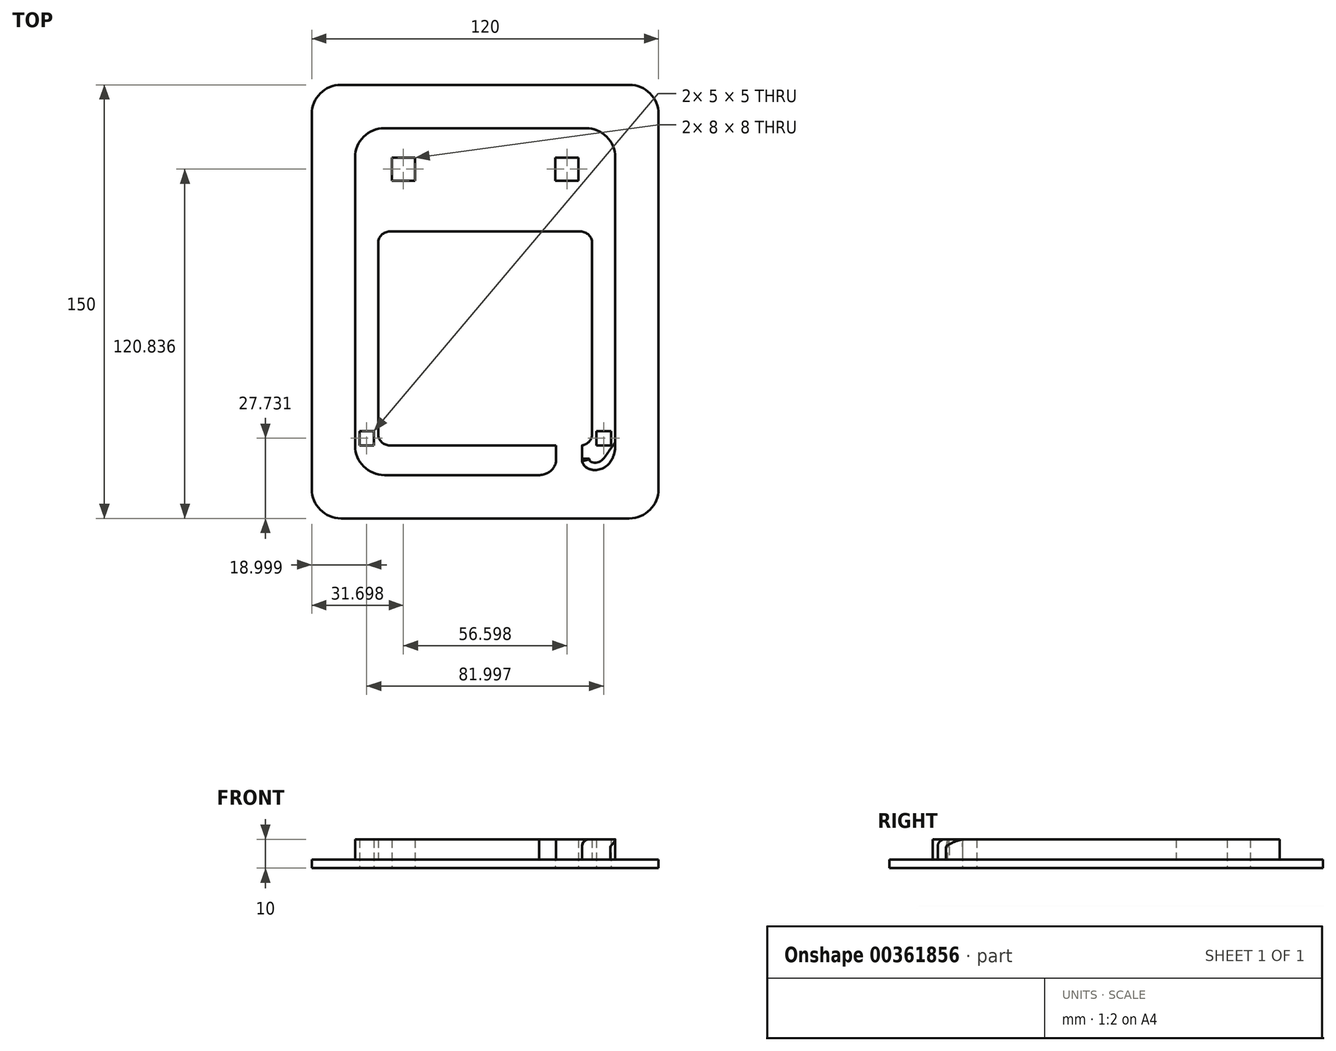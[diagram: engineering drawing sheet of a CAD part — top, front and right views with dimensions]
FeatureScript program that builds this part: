
annotation { "Feature Type Name" : "Feature", "Feature Type Description" : "" }
export const myFeature = defineFeature(function(context is Context, id is Id, definition is map)
    precondition{}
    {
        {
            var Q0;
            Q0=qCreatedBy(makeId("Top.planeOp"),FACE);
            var sketch = newSketch(context, id + "F0", { "sketchPlane" : qUnion([Q0])});
            skLineSegment(sketch, "E0", {"start": v(-11.46, -28.66) * mm, "end": v(-11.46, -18.43) * mm, "construction": true});
            skArc(sketch, "E1.0", {"start": v(28.36, -28.66) * mm, "mid": v(33.6, -27.2) * mm, "end": v(37.34, -23.25) * mm});
            skFitSpline(sketch, "E1.1", {"points": [v(27, -22.97) * mm, v(27, -23.26) * mm, v(27.03, -23.7) * mm, v(27.19, -24.26) * mm, v(27.36, -24.67) * mm, v(27.57, -25.04) * mm, v(27.93, -25.51) * mm, v(28.35, -25.9) * mm, v(28.84, -26.24) * mm, v(29.23, -26.44) * mm, v(29.63, -26.6) * mm, v(30.19, -26.79) * mm, v(30.9, -26.92) * mm, v(31.78, -26.94) * mm, v(32.64, -26.83) * mm, v(33.5, -26.6) * mm, v(34.3, -26.27) * mm, v(35.05, -25.83) * mm, v(35.74, -25.3) * mm, v(36.36, -24.7) * mm, v(36.9, -24) * mm, v(37.2, -23.5) * mm, v(37.34, -23.25) * mm]});
            skLineSegment(sketch, "E1.2", {"start": v(-43.48, -14.43) * mm, "end": v(-43.48, 51.57) * mm});
            skArc(sketch, "E1.3", {"start": v(-56.32, 106.34) * mm, "mid": v(-63.5, 103.36) * mm, "end": v(-66.48, 96.18) * mm});
            skArc(sketch, "E1.4", {"start": v(43.36, -43.66) * mm, "mid": v(50.54, -40.69) * mm, "end": v(53.52, -33.5) * mm});
            skLineSegment(sketch, "E1.5", {"start": v(-39.48, 51.57) * mm, "end": v(-43.48, 51.57) * mm});
            skArc(sketch, "E1.6", {"start": v(-66.48, -33.5) * mm, "mid": v(-63.5, -40.69) * mm, "end": v(-56.32, -43.66) * mm});
            skArc(sketch, "E1.7", {"start": v(-41.32, 91.34) * mm, "mid": v(-48.5, 88.36) * mm, "end": v(-51.48, 81.18) * mm});
            skLineSegment(sketch, "E1.8", {"start": v(18.05, -23.58) * mm, "end": v(25.68, -23.58) * mm});
            skArc(sketch, "E1.9", {"start": v(38.52, 81.18) * mm, "mid": v(35.54, 88.36) * mm, "end": v(28.36, 91.34) * mm});
            skArc(sketch, "E1.10", {"start": v(-51.48, -18.5) * mm, "mid": v(-48.5, -25.69) * mm, "end": v(-41.32, -28.66) * mm});
            skLineSegment(sketch, "E2.0.0", {"start": v(-66.48, 96.18) * mm, "end": v(-66.48, -33.5) * mm});
            skLineSegment(sketch, "E2.0.2", {"start": v(-56.32, -43.66) * mm, "end": v(43.36, -43.66) * mm});
            skLineSegment(sketch, "E2.0.4", {"start": v(53.52, -33.5) * mm, "end": v(53.52, 96.18) * mm});
            skArc(sketch, "E2.0.5", {"start": v(53.52, 96.18) * mm, "mid": v(50.54, 103.36) * mm, "end": v(43.36, 106.34) * mm});
            skLineSegment(sketch, "E2.0.6", {"start": v(43.36, 106.34) * mm, "end": v(-56.32, 106.34) * mm});
            skLineSegment(sketch, "E3.0.0", {"start": v(27, -18.4) * mm, "end": v(27, -22.97) * mm});
            skFitSpline(sketch, "E3.0.1", {"points": [v(27, -22.97) * mm, v(27, -23.26) * mm, v(27.03, -23.7) * mm, v(27.19, -24.26) * mm, v(27.36, -24.67) * mm, v(27.57, -25.04) * mm, v(27.93, -25.51) * mm, v(28.35, -25.9) * mm, v(28.84, -26.24) * mm, v(29.23, -26.44) * mm, v(29.63, -26.6) * mm, v(30.19, -26.79) * mm, v(30.9, -26.92) * mm, v(31.78, -26.94) * mm, v(32.64, -26.83) * mm, v(33.5, -26.6) * mm, v(34.3, -26.27) * mm, v(35.05, -25.83) * mm, v(35.74, -25.3) * mm, v(36.36, -24.7) * mm, v(36.9, -24) * mm, v(37.2, -23.5) * mm, v(37.34, -23.25) * mm]});
            skArc(sketch, "E3.0.2", {"start": v(37.34, -23.25) * mm, "mid": v(38.22, -20.95) * mm, "end": v(38.52, -18.5) * mm});
            skLineSegment(sketch, "E3.0.3", {"start": v(38.52, -18.5) * mm, "end": v(38.52, 81.18) * mm});
            skLineSegment(sketch, "E3.0.5", {"start": v(28.36, 91.34) * mm, "end": v(-41.32, 91.34) * mm});
            skLineSegment(sketch, "E3.0.7", {"start": v(-51.48, 81.18) * mm, "end": v(-51.48, -18.5) * mm});
            skLineSegment(sketch, "E3.0.9", {"start": v(-41.32, -28.66) * mm, "end": v(12.19, -28.66) * mm});
            skFitSpline(sketch, "E3.0.10", {"points": [v(12.19, -28.66) * mm, v(12.54, -28.66) * mm, v(13.07, -28.61) * mm, v(13.76, -28.46) * mm, v(14.27, -28.3) * mm, v(14.77, -28.1) * mm, v(15.24, -27.85) * mm, v(15.69, -27.57) * mm, v(16.12, -27.24) * mm, v(16.52, -26.89) * mm, v(16.88, -26.5) * mm, v(17.2, -26.09) * mm, v(17.5, -25.63) * mm, v(17.73, -25.15) * mm, v(17.9, -24.65) * mm, v(18.02, -24.12) * mm, v(18.05, -23.76) * mm, v(18.05, -23.58) * mm]});
            skLineSegment(sketch, "E3.0.11", {"start": v(18.05, -23.58) * mm, "end": v(18.05, -18.43) * mm});
            skLineSegment(sketch, "E3.0.12", {"start": v(18.05, -18.43) * mm, "end": v(-39.48, -18.43) * mm});
            skArc(sketch, "E3.0.13", {"start": v(-39.48, -18.43) * mm, "mid": v(-42.31, -17.26) * mm, "end": v(-43.48, -14.43) * mm});
            skArc(sketch, "E3.0.15", {"start": v(-43.48, 51.57) * mm, "mid": v(-42.31, 54.4) * mm, "end": v(-39.48, 55.57) * mm});
            skLineSegment(sketch, "E3.0.16", {"start": v(-39.48, 55.57) * mm, "end": v(26.52, 55.57) * mm});
            skArc(sketch, "E3.0.17", {"start": v(26.52, 55.57) * mm, "mid": v(29.35, 54.4) * mm, "end": v(30.52, 51.57) * mm});
            skLineSegment(sketch, "E3.0.18", {"start": v(30.52, 51.57) * mm, "end": v(30.52, -14.43) * mm});
            skArc(sketch, "E3.0.19", {"start": v(30.52, -14.43) * mm, "mid": v(29.5, -17.08) * mm, "end": v(27, -18.4) * mm});
            skLineSegment(sketch, "E4.0.0", {"start": v(-38.78, 81.18) * mm, "end": v(-38.78, 73.18) * mm});
            skLineSegment(sketch, "E4.0.1", {"start": v(-38.78, 73.18) * mm, "end": v(-30.78, 73.18) * mm});
            skLineSegment(sketch, "E4.0.2", {"start": v(-30.78, 73.18) * mm, "end": v(-30.78, 81.18) * mm});
            skLineSegment(sketch, "E4.0.3", {"start": v(-30.78, 81.18) * mm, "end": v(-38.78, 81.18) * mm});
            skLineSegment(sketch, "E5.0.0", {"start": v(25.82, 73.18) * mm, "end": v(25.82, 81.18) * mm});
            skLineSegment(sketch, "E5.0.1", {"start": v(25.82, 81.18) * mm, "end": v(17.82, 81.18) * mm});
            skLineSegment(sketch, "E5.0.2", {"start": v(17.82, 81.18) * mm, "end": v(17.82, 73.18) * mm});
            skLineSegment(sketch, "E5.0.3", {"start": v(17.82, 73.18) * mm, "end": v(25.82, 73.18) * mm});
            skLineSegment(sketch, "E6.0.0", {"start": v(-44.98, -18.43) * mm, "end": v(-44.98, -13.43) * mm});
            skLineSegment(sketch, "E6.0.1", {"start": v(-44.98, -13.43) * mm, "end": v(-49.98, -13.43) * mm});
            skLineSegment(sketch, "E6.0.2", {"start": v(-49.98, -13.43) * mm, "end": v(-49.98, -18.43) * mm});
            skLineSegment(sketch, "E6.0.3", {"start": v(-49.98, -18.43) * mm, "end": v(-44.98, -18.43) * mm});
            skLineSegment(sketch, "E7.0.0", {"start": v(32.02, -13.43) * mm, "end": v(32.02, -18.43) * mm});
            skLineSegment(sketch, "E7.0.1", {"start": v(32.02, -18.43) * mm, "end": v(37.02, -18.43) * mm});
            skLineSegment(sketch, "E7.0.2", {"start": v(37.02, -18.43) * mm, "end": v(37.02, -13.43) * mm});
            skLineSegment(sketch, "E7.0.3", {"start": v(37.02, -13.43) * mm, "end": v(32.02, -13.43) * mm});
            skSolve(sketch);
        }
        {
            var Q0;
            Q0=makeQuery(id+"F0.imprint","IMPRINT",FACE,{"disambiguationData":[TD([[makeQuery(id+"F0.imprint","IMPRINT",EDGE,{"derivedFrom":sQuery(id+"F0.wireOp",EDGE,"E2.0.0")}),1.0]])]});
            extrude(context, id + "F1", {"entities" : qUnion([Q0]), "depth" : 3 * mm, "offsetDistance" : 25.4 * mm});
        }
        {
            var Q0;
            Q0=makeQuery(id+"F0.imprint","IMPRINT",FACE,{"disambiguationData":[TD([[makeQuery(id+"F0.imprint","IMPRINT",EDGE,{"derivedFrom":sQuery(id+"F0.wireOp",EDGE,"E3.0.0")}),1.0]])]});
            extrude(context, id + "F2", {"entities" : qUnion([Q0]), "operationType" : NewBodyOperationType.ADD, "depth" : 10 * mm, "offsetDistance" : 25.4 * mm});
        }
        {
            var Q0;
            Q0=makeQuery(id+"F2.opExtrude","CAP_EDGE",EDGE,{"disambiguationData":[OSD([sQuery(id+"F0.wireOp",EDGE,"E3.0.0")])],"isStart":false});
            fillet(context, id + "F3", {"entities" : qUnion([Q0]), "radius" : 2.54 * mm, "tangentPropagation" : true, "allowEdgeOverflow" : false});
        }
    });
